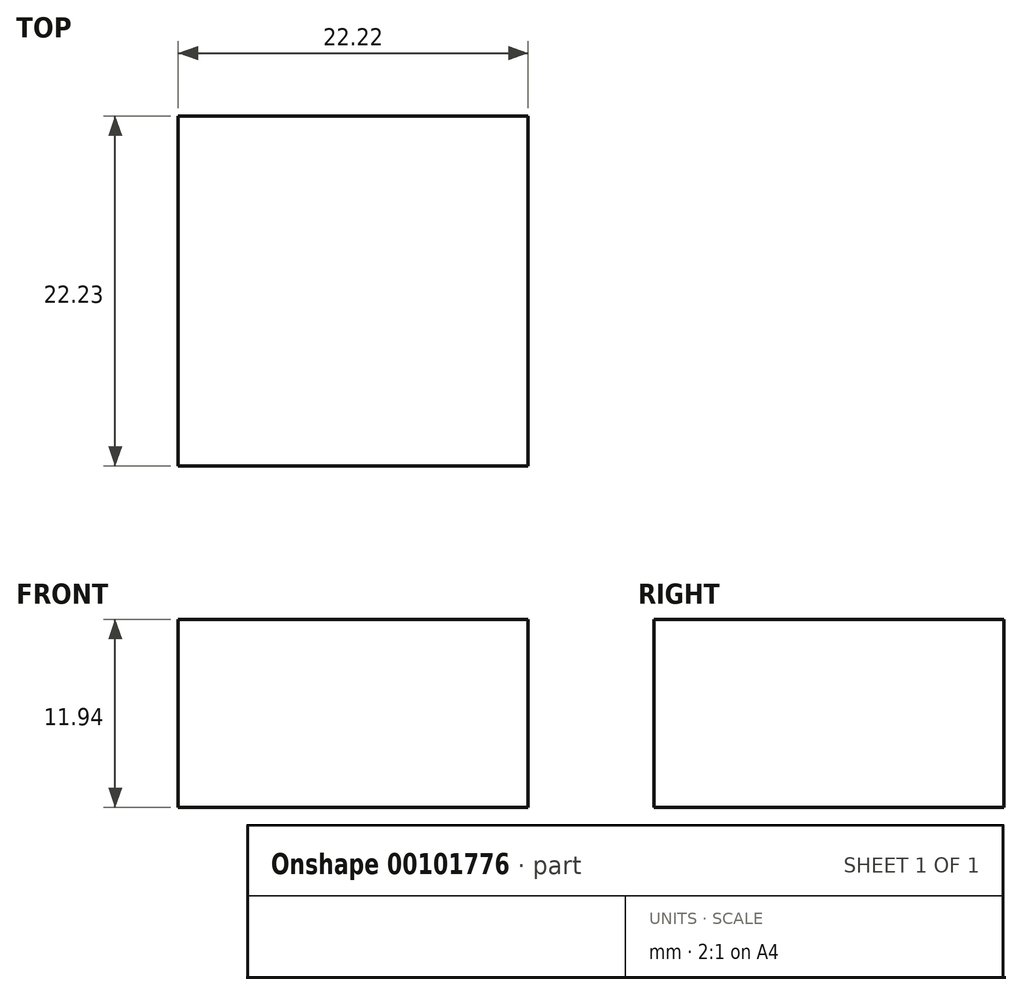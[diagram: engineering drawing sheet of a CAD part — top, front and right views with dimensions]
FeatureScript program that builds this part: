
annotation { "Feature Type Name" : "Feature", "Feature Type Description" : "" }
export const myFeature = defineFeature(function(context is Context, id is Id, definition is map)
    precondition{}
    {
        {
            var Q0;
            Q0=qCreatedBy(makeId("Front.planeOp"),FACE);
            var sketch = newSketch(context, id + "F0", { "sketchPlane" : qUnion([Q0])});
            skLineSegment(sketch, "E0.bottom", {"start": v(-10.68, 10.59) * mm, "end": v(11.54, 10.59) * mm});
            skLineSegment(sketch, "E0.top", {"start": v(-10.68, -1.35) * mm, "end": v(11.54, -1.35) * mm});
            skLineSegment(sketch, "E0.left", {"start": v(-10.68, 10.59) * mm, "end": v(-10.68, -1.35) * mm});
            skLineSegment(sketch, "E0.right", {"start": v(11.54, 10.59) * mm, "end": v(11.54, -1.35) * mm});
            skSolve(sketch);
        }
        {
            var Q0;
            Q0=makeQuery(id+"F0.imprint","IMPRINT",FACE,{"disambiguationData":[TD([[makeQuery(id+"F0.imprint","IMPRINT",EDGE,{"derivedFrom":sQuery(id+"F0.wireOp",EDGE,"E0.bottom")}),-1.0]])]});
            extrude(context, id + "F1", {"entities" : qUnion([Q0]), "depth" : 22.22 * mm});
        }
    });
